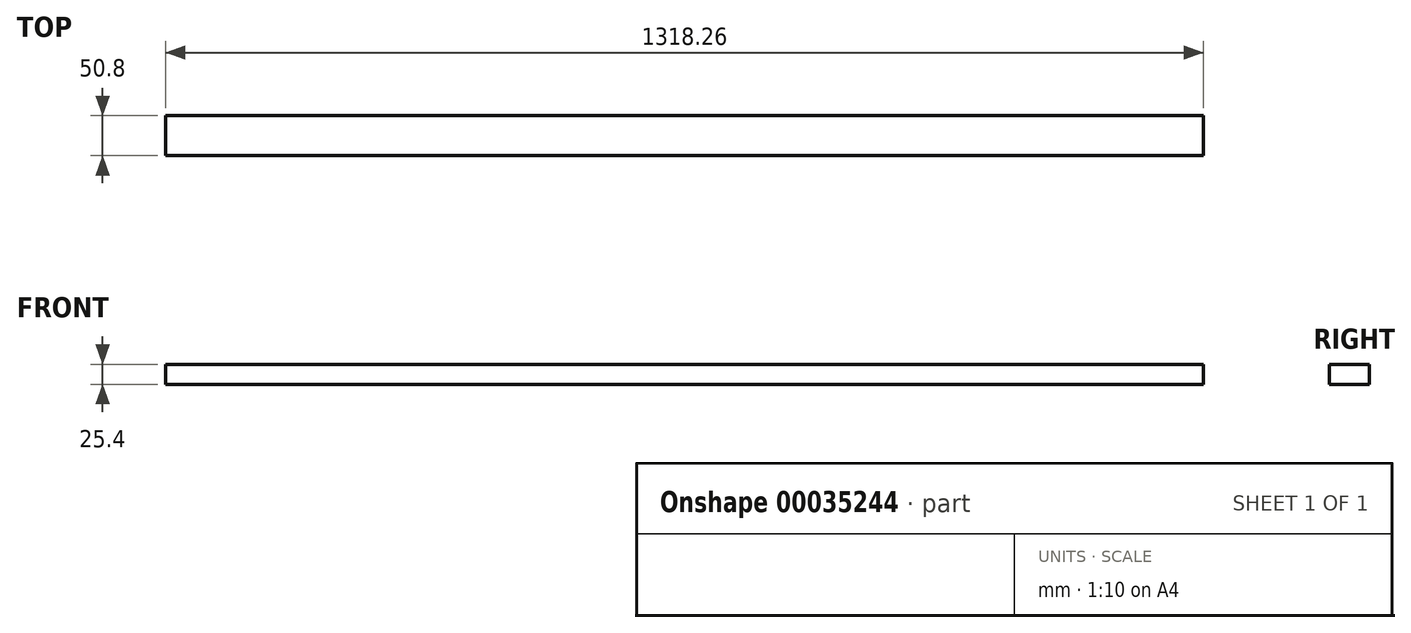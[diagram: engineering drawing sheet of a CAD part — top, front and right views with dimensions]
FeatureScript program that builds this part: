
annotation { "Feature Type Name" : "Feature", "Feature Type Description" : "" }
export const myFeature = defineFeature(function(context is Context, id is Id, definition is map)
    precondition{}
    {
        {
            var Q0;
            Q0=qCreatedBy(makeId("Top.planeOp"),FACE);
            var sketch = newSketch(context, id + "F0", { "sketchPlane" : qUnion([Q0])});
            skLineSegment(sketch, "E0.rect.bottom", {"start": v(659.13, -25.4) * mm, "end": v(-659.13, -25.4) * mm});
            skLineSegment(sketch, "E0.rect.top", {"start": v(659.13, 25.4) * mm, "end": v(-659.13, 25.4) * mm});
            skLineSegment(sketch, "E0.rect.left", {"start": v(659.13, -25.4) * mm, "end": v(659.13, 25.4) * mm});
            skLineSegment(sketch, "E0.rect.right", {"start": v(-659.13, -25.4) * mm, "end": v(-659.13, 25.4) * mm});
            skPoint(sketch, "E0.rect.middle", {"position": v(0, 0) * mm});
            skSolve(sketch);
        }
        {
            var Q0;
            Q0=makeQuery(id+"F0.imprint","IMPRINT",FACE,{"disambiguationData":[TD([[makeQuery(id+"F0.imprint","IMPRINT",EDGE,{"derivedFrom":sQuery(id+"F0.wireOp",EDGE,"E0.rect.bottom")}),-1.0]])]});
            extrude(context, id + "F1", {"entities" : qUnion([Q0]), "depth" : 25.4 * mm});
        }
    });
